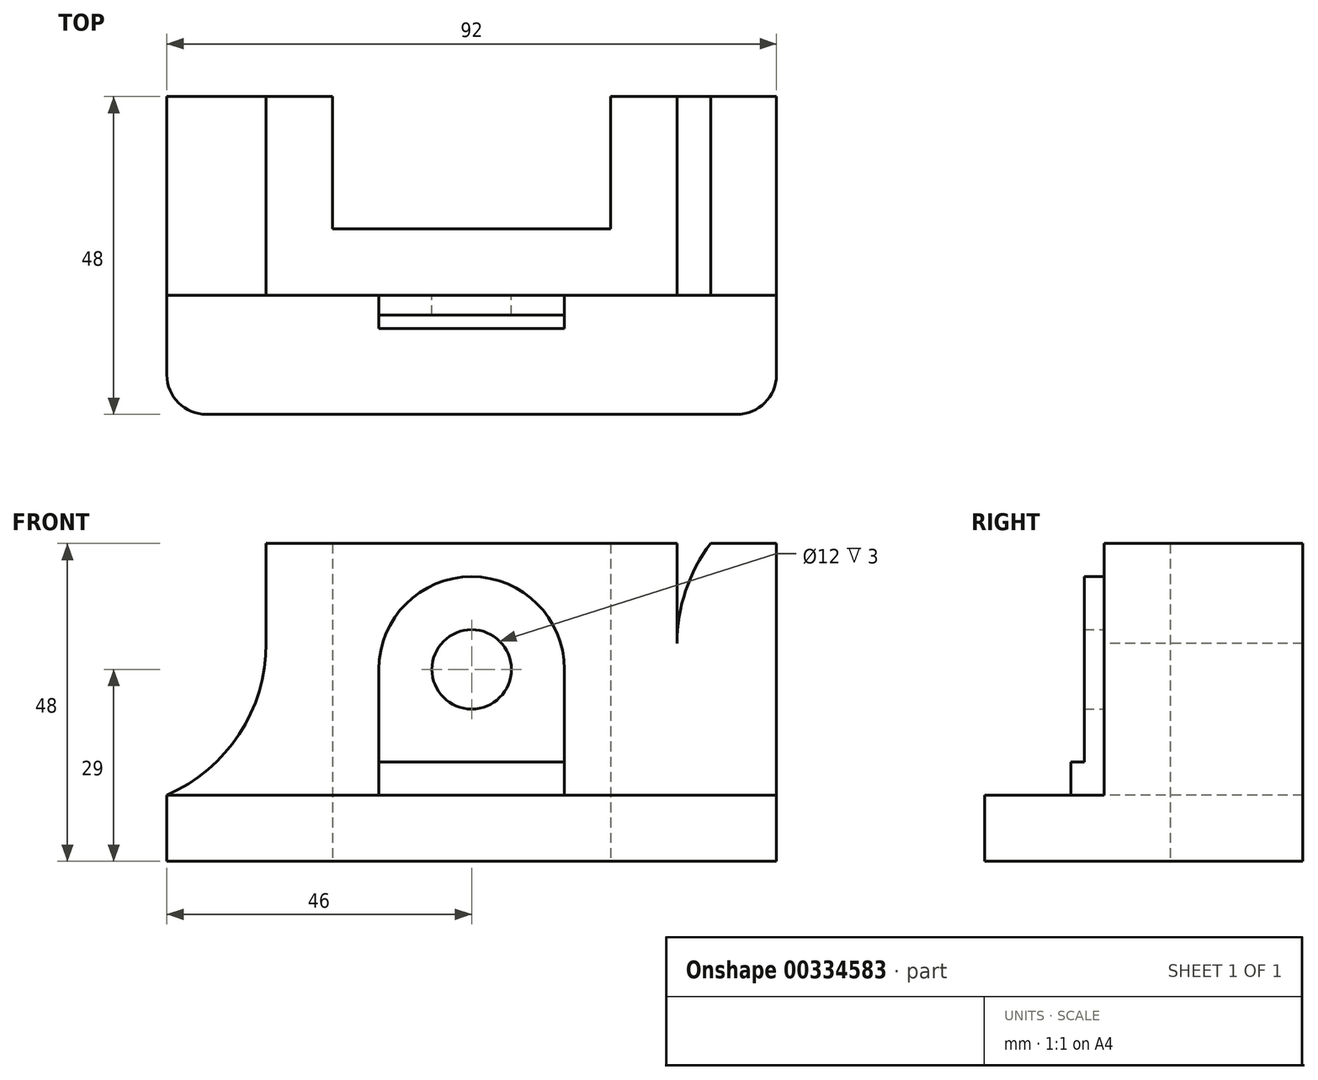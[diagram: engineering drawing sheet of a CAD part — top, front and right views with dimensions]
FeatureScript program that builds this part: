
annotation { "Feature Type Name" : "Feature", "Feature Type Description" : "" }
export const myFeature = defineFeature(function(context is Context, id is Id, definition is map)
    precondition{}
    {
        {
            var Q0;
            Q0=qCreatedBy(makeId("Top.planeOp"),FACE);
            var sketch = newSketch(context, id + "F0", { "sketchPlane" : qUnion([Q0])});
            skLineSegment(sketch, "E0.bottom", {"start": v(-46, 30) * mm, "end": v(46, 30) * mm});
            skLineSegment(sketch, "E0.top", {"start": v(-46, -18) * mm, "end": v(46, -18) * mm});
            skLineSegment(sketch, "E0.left", {"start": v(-46, 30) * mm, "end": v(-46, -18) * mm});
            skLineSegment(sketch, "E0.right", {"start": v(46, 30) * mm, "end": v(46, -18) * mm});
            skPoint(sketch, "E0.middle", {"position": v(0, 0) * mm});
            skLineSegment(sketch, "E1.bottom", {"start": v(-21, 36.76) * mm, "end": v(21, 36.76) * mm});
            skLineSegment(sketch, "E1.top", {"start": v(-21, 10) * mm, "end": v(21, 10) * mm});
            skLineSegment(sketch, "E1.left", {"start": v(-21, 36.76) * mm, "end": v(-21, 10) * mm});
            skLineSegment(sketch, "E1.right", {"start": v(21, 36.76) * mm, "end": v(21, 10) * mm});
            skLineSegment(sketch, "E2", {"start": v(-46, 0) * mm, "end": v(46, 0) * mm});
            skSolve(sketch);
        }
        {
            var Q0;
            {var subQ8=sQuery(id+"F0.wireOp",EDGE,"E1.top");Q0=makeQuery(id+"F0.imprint","IMPRINT",FACE,{"disambiguationData":[TD([[makeQuery(id+"F0.imprint","IMPRINT",EDGE,{"derivedFrom":subQ8}),-1.0]])]});}
            extrude(context, id + "F1", {"entities" : qUnion([Q0]), "depth" : 48 * mm});
        }
        {
            var Q0;
            {var subQ0=sQuery(id+"F0.wireOp",EDGE,"E0.top");Q0=makeQuery(id+"F0.imprint","IMPRINT",FACE,{"disambiguationData":[TD([[makeQuery(id+"F0.imprint","IMPRINT",EDGE,{"derivedFrom":subQ0}),1.0]])]});}
            extrude(context, id + "F2", {"entities" : qUnion([Q0]), "operationType" : NewBodyOperationType.ADD, "depth" : 10 * mm});
        }
        {
            var Q0;
            Q0=qCreatedBy(makeId("Front.planeOp"),FACE);
            var sketch = newSketch(context, id + "F3", { "sketchPlane" : qUnion([Q0])});
            skLineSegment(sketch, "E3", {"start": v(-31, 81.63) * mm, "end": v(-31, 0) * mm});
            skCircle(sketch, "E4", {"center": v(-56, 32.91) * mm, "radius": 25 * mm});
            skPoint(sketch, "E4.first.point", {"position": v(-31, 32.91) * mm});
            skLineSegment(sketch, "E5", {"start": v(-46.42, 56) * mm, "end": v(-31, 56) * mm});
            skLineSegment(sketch, "E6.MirrorCS", {"start": v(46.42, 56) * mm, "end": v(31, 56) * mm});
            skLineSegment(sketch, "E7.MirrorCS", {"start": v(31, 81.63) * mm, "end": v(31, 0) * mm});
            skPoint(sketch, "E8.MirrorP", {"position": v(31, 32.91) * mm});
            skCircle(sketch, "E9.MirrorC", {"center": v(56, 32.91) * mm, "radius": 25 * mm});
            skSolve(sketch);
        }
        {
            var Q0;
            {var subQ0=sQuery(id+"F3.wireOp",EDGE,"E5");Q0=makeQuery(id+"F3.imprint","IMPRINT",FACE,{"disambiguationData":[TD([[makeQuery(id+"F3.imprint","IMPRINT",EDGE,{"derivedFrom":subQ0}),-1.0]])]});}
            var Q1;
            {var subQ0=sQuery(id+"F3.wireOp",EDGE,"E4");var subQ1=makeQuery(id+"F3.imprint","INTERSECT",VERTEX,{"derivedFrom":[subQ0,sQuery(id+"F3.wireOp",EDGE,"E5")]});Q1=makeQuery(id+"F3.imprint","IMPRINT",FACE,{"disambiguationData":[TD([[makeQuery(id+"F3.imprint","IMPRINT",EDGE,{"disambiguationData":[TD([[subQ1,1.0]])],"derivedFrom":subQ0}),1.0]])]});}
            var Q2;
            {var subQ0=sQuery(id+"F3.wireOp",EDGE,"E9.MirrorC");var subQ1=makeQuery(id+"F3.imprint","INTERSECT",VERTEX,{"derivedFrom":[sQuery(id+"F3.wireOp",EDGE,"E6.MirrorCS"),subQ0]});Q2=makeQuery(id+"F3.imprint","IMPRINT",FACE,{"disambiguationData":[TD([[makeQuery(id+"F3.imprint","IMPRINT",EDGE,{"disambiguationData":[TD([[subQ1,1.0]])],"derivedFrom":subQ0}),-1.0]])]});}
            var Q3;
            {var subQ0=sQuery(id+"F3.wireOp",EDGE,"E6.MirrorCS");Q3=makeQuery(id+"F3.imprint","IMPRINT",FACE,{"disambiguationData":[TD([[makeQuery(id+"F3.imprint","IMPRINT",EDGE,{"derivedFrom":subQ0}),1.0]])]});}
            extrude(context, id + "F4", {"entities" : qUnion([Q0, Q1, Q2, Q3]), "operationType" : NewBodyOperationType.REMOVE, "oppositeDirection" : true, "depth" : 42.2 * mm});
        }
        {
            var Q0;
            Q0=makeQuery(id+"F1.opExtrude","SWEPT_FACE",FACE,{"disambiguationData":[OSD([sQuery(id+"F0.wireOp",EDGE,"E2")])]});
            var sketch = newSketch(context, id + "F5", { "sketchPlane" : qUnion([Q0])});
            skArc(sketch, "E10", {"start": v(14, 29) * mm, "mid": v(0, 43) * mm, "end": v(-14, 29) * mm});
            skCircle(sketch, "E11", {"center": v(0, 29) * mm, "radius": 6 * mm});
            skLineSegment(sketch, "E12", {"start": v(-14, 29) * mm, "end": v(-14, 10) * mm});
            skLineSegment(sketch, "E13", {"start": v(14, 29) * mm, "end": v(14, 10) * mm});
            skLineSegment(sketch, "E14", {"start": v(14, 10) * mm, "end": v(-14, 10) * mm});
            skLineSegment(sketch, "E15", {"start": v(-14, 15) * mm, "end": v(14, 15) * mm});
            skSolve(sketch);
        }
        {
            var Q0;
            {var subQ1=sQuery(id+"F5.wireOp",EDGE,"E10");Q0=makeQuery(id+"F5.imprint","IMPRINT",FACE,{"disambiguationData":[TD([[makeQuery(id+"F5.imprint","IMPRINT",EDGE,{"derivedFrom":subQ1}),1.0]])]});}
            extrude(context, id + "F6", {"entities" : qUnion([Q0]), "operationType" : NewBodyOperationType.ADD, "depth" : 3 * mm});
        }
        {
            var Q0;
            {var subQ0=sQuery(id+"F5.wireOp",EDGE,"E14");Q0=makeQuery(id+"F5.imprint","IMPRINT",FACE,{"disambiguationData":[TD([[makeQuery(id+"F5.imprint","IMPRINT",EDGE,{"derivedFrom":subQ0}),1.0]])]});}
            extrude(context, id + "F7", {"entities" : qUnion([Q0]), "operationType" : NewBodyOperationType.ADD, "depth" : 5 * mm});
        }
        {
            var Q0;
            Q0=makeQuery(id+"F2.opExtrude","SWEPT_EDGE",EDGE,{"disambiguationData":[OSD([sQuery(id+"F0.wireOp",EDGE,"E0.top"),sQuery(id+"F0.wireOp",EDGE,"E0.left")])]});
            var Q1;
            Q1=makeQuery(id+"F2.opExtrude","SWEPT_EDGE",EDGE,{"disambiguationData":[OSD([sQuery(id+"F0.wireOp",EDGE,"E0.top"),sQuery(id+"F0.wireOp",EDGE,"E0.right")])]});
            fillet(context, id + "F8", {"entities" : qUnion([Q0, Q1]), "radius" : 6 * mm, "tangentPropagation" : true, "allowEdgeOverflow" : false});
        }
    });
